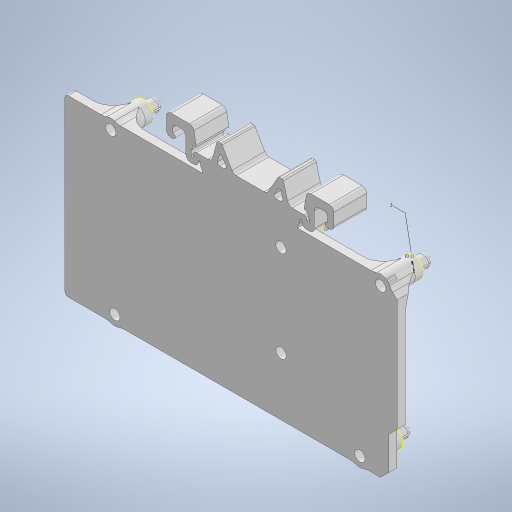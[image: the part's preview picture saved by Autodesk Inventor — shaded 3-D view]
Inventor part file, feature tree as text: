
AUTODESK INVENTOR PART (.ipt)
format: ipt  version: 2023 (Build 270158030, 158C)  size: 978,432 bytes
history: native  units: mm
features: other x20, fillet x8, reference x7, extrude x6, sketch x5, projected_geometry x2
ambient origin geometry x8: Origin, YZ Plane, XZ Plane, XY Plane, X Axis, Y Axis, Z Axis, Center Point
bodies: Body1 (feature_tree)
feature tree (48):
  other  "backplate"
  other  "Blocks"
  extrude  "Extrusion1"  Depth=1.5mm
  extrude  "Extrusion2"  Depth=2.5mm TaperAngle=0.0deg
  fillet  "Fillet2"  Radius=5.0mm
  extrude  "Extrusion3"  Depth=2.0mm
  fillet  "Fillet4"  Radius=5.0mm
  fillet  "Fillet5"  Radius=3.0mm
  sketch  "Sketch4"  dims[d15=0.1mm d16=2.0mm d17=0.0mm]
  extrude  "Extrusion4"  Depth=2.0mm TaperAngle=0.0deg
  extrude  "Extrusion5"  Depth=1.0mm
  other  "Work Axis1"
  other  "Work Axis2"
  other  "Work Axis3"
  other  "Work Axis4"
  other  "Work Axis5"
  other  "Work Axis6"
  extrude  "Extrusion6"  Depth=1.0mm TaperAngle=0.0deg
  fillet  "Fillet6"  Radius=1.0mm
  fillet  "Fillet7"  Radius=1.759846mm
  fillet  "Fillet8"  Radius=1.271846mm
  fillet  "Fillet9"  Radius=3.0mm
  fillet  "Fillet10"  [1 undecoded]
  sketch  "Sketch1"  dims[d0=6.2mm d1=1.5mm]
  reference  "Reference1"
  reference  "Reference2"
  reference  "Reference3"
  reference  "Reference4"
  reference  "Reference5"
  reference  "Reference6"
  sketch  "Sketch2"  dims[d2=10.0mm d3=0.0mm d4=2.5mm d5=0.0mm d7=5.0mm]
  reference  "Reference7"
  sketch  "Sketch3"  dims[d9=10.0mm d10=0.0mm d12=2.0mm d13=5.0mm d14=3.0mm]
  other  "din-rail-clip-outline"
  projected_geometry  "Projected Loop1"
  projected_geometry  "Projected Loop2"
  sketch  "Sketch6"  dims[d18=4.0mm d19=1.22173mm d21=0.4mm d25=3.0mm d26=0.0mm d27=1.0mm d30=1.759846mm d31=1.271846mm d32=3.0mm d33=0.0mm d34=36.0mm d35=7.0mm d36=2.0mm d37=5.0mm d38=1.0mm d28=0.5mm d29=0.872665mm]
  other  "crosscut"
  other  "Block3"
  other  "arduino-DIN-mount.iam"
  other  "arduinoMegaDetailed:1"
  other  "crosscut:1"
  other  "crosscut:2"
  other  "crosscut:3"
  other  "crosscut:4"
  other  "crosscut:5"
  other  "crosscut:6"
  other  "Block3:1"
note: 1 required parameter value undecoded (feature->parameter linkage not recoverable at this tier; creation-order binding heuristic only, values carry confidence <= 0.55)
